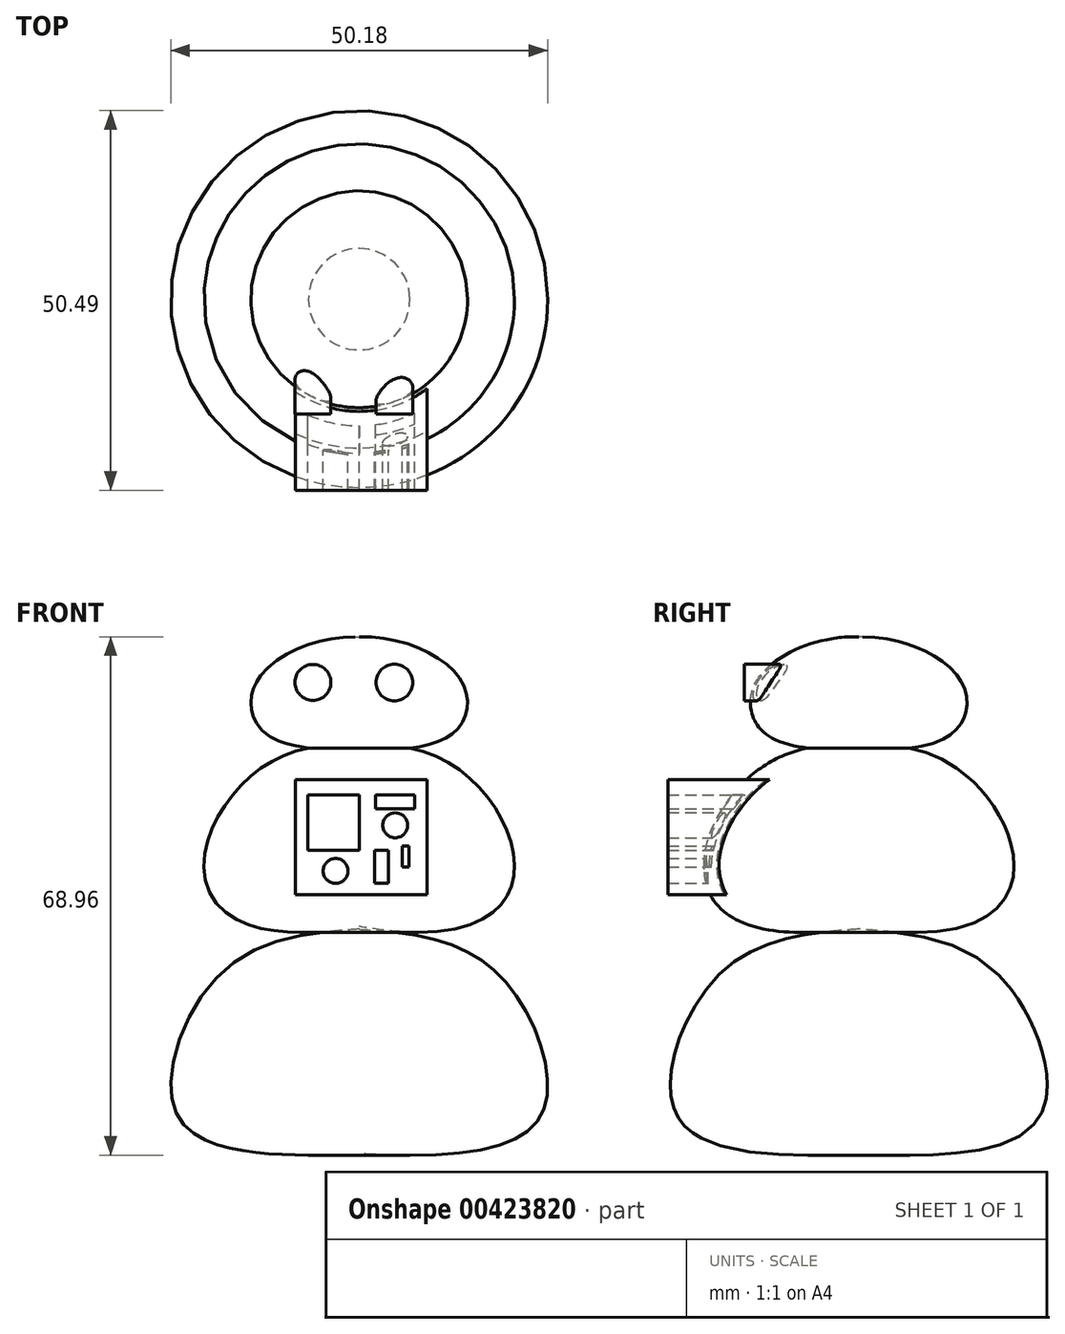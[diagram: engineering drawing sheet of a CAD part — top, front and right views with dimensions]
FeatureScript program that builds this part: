
annotation { "Feature Type Name" : "Feature", "Feature Type Description" : "" }
export const myFeature = defineFeature(function(context is Context, id is Id, definition is map)
    precondition{}
    {
        {
            var Q0;
            Q0=qCreatedBy(makeId("Front.planeOp"),FACE);
            var sketch = newSketch(context, id + "F0", { "sketchPlane" : qUnion([Q0])});
            skLineSegment(sketch, "E0", {"start": v(0, 46.83) * mm, "end": v(0, -37.24) * mm});
            skFitSpline(sketch, "E1", {"points": [v(0, 29.87) * mm, v(19.88, 22.4) * mm, v(24.4, 5.54) * mm, v(0, 0) * mm], "startDerivative": vector(88.45, -5.13) * mm, "endDerivative": vector(-107.1, 5.39) * mm});
            skSolve(sketch);
        }
        {
            var Q0;
            {var subQ0=sQuery(id+"F0.wireOp",EDGE,"E1");Q0=makeQuery(id+"F0.imprint","IMPRINT",FACE,{"disambiguationData":[TD([[makeQuery(id+"F0.imprint","IMPRINT",EDGE,{"derivedFrom":subQ0}),-1.0]])]});}
            var Q1;
            Q1=sQuery(id+"F0.wireOp",EDGE,"E0");
            revolve(context, id + "F1", {"entities" : qUnion([Q0]), "axis" : qUnion([Q1]), "revolveType" : RevolveType.FULL});
        }
        {
            var Q0;
            Q0=qCreatedBy(makeId("Front.planeOp"),FACE);
            var sketch = newSketch(context, id + "F2", { "sketchPlane" : qUnion([Q0])});
            skFitSpline(sketch, "E2", {"points": [v(0, 53.83) * mm, v(16.35, 48.3) * mm, v(20.38, 35.98) * mm, v(0, 30.23) * mm], "startDerivative": vector(62.4, 13.34) * mm, "endDerivative": vector(-104.52, 18.87) * mm});
            skLineSegment(sketch, "E3", {"start": v(0, 59.73) * mm, "end": v(0, -41.3) * mm});
            skLineSegment(sketch, "E4", {"start": v(0.37, -40.19) * mm, "end": v(0, -41.3) * mm});
            skSolve(sketch);
        }
        {
            var Q0;
            {var subQ0=sQuery(id+"F2.wireOp",EDGE,"E2");Q0=makeQuery(id+"F2.imprint","IMPRINT",FACE,{"disambiguationData":[TD([[makeQuery(id+"F2.imprint","IMPRINT",EDGE,{"derivedFrom":subQ0}),-1.0]])]});}
            var Q1;
            Q1=sQuery(id+"F2.wireOp",EDGE,"E3");
            revolve(context, id + "F3", {"entities" : qUnion([Q0]), "axis" : qUnion([Q1]), "revolveType" : RevolveType.FULL});
        }
        {
            var Q0;
            Q0=qCreatedBy(makeId("Front.planeOp"),FACE);
            var sketch = newSketch(context, id + "F4", { "sketchPlane" : qUnion([Q0])});
            skLineSegment(sketch, "E5", {"start": v(0, 74.85) * mm, "end": v(0, -43.14) * mm});
            skFitSpline(sketch, "E6", {"points": [v(0, 68.76) * mm, v(13.72, 62.68) * mm, v(12.62, 56.04) * mm, v(0, 53.65) * mm], "startDerivative": vector(45.1, 1.43) * mm, "endDerivative": vector(-42.53, -0.45) * mm});
            skSolve(sketch);
        }
        {
            var Q0;
            Q0 = qSketchRegion(id + "F4", true);
            var Q1;
            Q1=sQuery(id+"F4.wireOp",EDGE,"E5");
            revolve(context, id + "F5", {"operationType" : NewBodyOperationType.ADD, "entities" : qUnion([Q0]), "axis" : qUnion([Q1]), "revolveType" : RevolveType.FULL});
        }
        {
            var Q0;
            Q0=qCreatedBy(makeId("Front.planeOp"),FACE);
            var sketch = newSketch(context, id + "F6", { "sketchPlane" : qUnion([Q0])});
            skCircle(sketch, "E7", {"center": v(-6.16, 62.7) * mm, "radius": 2.4 * mm});
            skCircle(sketch, "E8", {"center": v(4.69, 62.68) * mm, "radius": 2.45 * mm});
            skSolve(sketch);
        }
        {
            var Q0;
            Q0 = qSketchRegion(id + "F6", true);
            extrude(context, id + "F7", {"entities" : qUnion([Q0]), "operationType" : NewBodyOperationType.ADD, "depth" : 15.24 * mm});
        }
        {
            var Q0;
            Q0=qCreatedBy(makeId("Front.planeOp"),FACE);
            var sketch = newSketch(context, id + "F8", { "sketchPlane" : qUnion([Q0])});
            skLineSegment(sketch, "E9.bottom", {"start": v(-8.48, 49.78) * mm, "end": v(9.03, 49.78) * mm});
            skLineSegment(sketch, "E9.top", {"start": v(-8.48, 34.47) * mm, "end": v(9.03, 34.47) * mm});
            skLineSegment(sketch, "E9.left", {"start": v(-8.48, 49.78) * mm, "end": v(-8.48, 34.47) * mm});
            skLineSegment(sketch, "E9.right", {"start": v(9.03, 49.78) * mm, "end": v(9.03, 34.47) * mm});
            skLineSegment(sketch, "E10.bottom", {"start": v(-6.82, 47.75) * mm, "end": v(0, 47.75) * mm});
            skLineSegment(sketch, "E10.top", {"start": v(-6.82, 40.37) * mm, "end": v(0, 40.37) * mm});
            skLineSegment(sketch, "E10.left", {"start": v(-6.82, 47.75) * mm, "end": v(-6.82, 40.37) * mm});
            skLineSegment(sketch, "E10.right", {"start": v(0, 47.75) * mm, "end": v(0, 40.37) * mm});
            skCircle(sketch, "E11", {"center": v(-5.35, 46.09) * mm, "radius": 1 * mm});
            skCircle(sketch, "E12", {"center": v(-5.35, 42.22) * mm, "radius": 1.1 * mm});
            skLineSegment(sketch, "E13.bottom", {"start": v(-2.77, 46.27) * mm, "end": v(-2.03, 46.27) * mm});
            skLineSegment(sketch, "E13.top", {"start": v(-2.77, 42.03) * mm, "end": v(-2.03, 42.03) * mm});
            skLineSegment(sketch, "E13.left", {"start": v(-2.77, 46.27) * mm, "end": v(-2.77, 42.03) * mm});
            skLineSegment(sketch, "E13.right", {"start": v(-2.03, 46.27) * mm, "end": v(-2.03, 42.03) * mm});
            skLineSegment(sketch, "E14.bottom", {"start": v(2.21, 47.75) * mm, "end": v(7.37, 47.75) * mm});
            skLineSegment(sketch, "E14.top", {"start": v(2.21, 45.9) * mm, "end": v(7.37, 45.9) * mm});
            skLineSegment(sketch, "E14.left", {"start": v(2.21, 47.75) * mm, "end": v(2.21, 45.9) * mm});
            skLineSegment(sketch, "E14.right", {"start": v(7.37, 47.75) * mm, "end": v(7.37, 45.9) * mm});
            skCircle(sketch, "E15", {"center": v(4.8, 43.7) * mm, "radius": 1.66 * mm});
            skPoint(sketch, "E15.centerSnap0", {"position": v(4.8, 45.9) * mm});
            skLineSegment(sketch, "E16.bottom", {"start": v(6.64, 40.93) * mm, "end": v(5.72, 40.93) * mm});
            skLineSegment(sketch, "E16.top", {"start": v(6.64, 38.16) * mm, "end": v(5.72, 38.16) * mm});
            skLineSegment(sketch, "E16.left", {"start": v(6.64, 40.93) * mm, "end": v(6.64, 38.16) * mm});
            skLineSegment(sketch, "E16.right", {"start": v(5.72, 40.93) * mm, "end": v(5.72, 38.16) * mm});
            skLineSegment(sketch, "E17.bottom", {"start": v(2.03, 40.37) * mm, "end": v(3.87, 40.37) * mm});
            skLineSegment(sketch, "E17.top", {"start": v(2.03, 35.95) * mm, "end": v(3.87, 35.95) * mm});
            skLineSegment(sketch, "E17.left", {"start": v(2.03, 40.37) * mm, "end": v(2.03, 35.95) * mm});
            skLineSegment(sketch, "E17.right", {"start": v(3.87, 40.37) * mm, "end": v(3.87, 35.95) * mm});
            skCircle(sketch, "E18", {"center": v(-6.82, 37.6) * mm, "radius": 1.66 * mm});
            skCircle(sketch, "E19", {"center": v(-3.13, 37.6) * mm, "radius": 1.66 * mm});
            skSolve(sketch);
        }
        {
            var Q0;
            Q0 = qSketchRegion(id + "F8", true);
            extrude(context, id + "F9", {"entities" : qUnion([Q0]), "operationType" : NewBodyOperationType.ADD, "depth" : 25.4 * mm});
        }
        {
            var Q0;
            Q0=qCreatedBy(makeId("Front.planeOp"),FACE);
            var sketch = newSketch(context, id + "F10", { "sketchPlane" : qUnion([Q0])});
            skFitSpline(sketch, "E20", {"points": [v(-9.56, 66.67) * mm, v(-6.54, 72.21) * mm, v(12.33, 72.97) * mm, v(14.6, 67.18) * mm, v(10.57, 68.18) * mm, v(12.33, 69.7) * mm, v(8.05, 71.2) * mm, v(6.04, 67.93) * mm, v(5.79, 68.94) * mm], "startDerivative": vector(7.3, 43.13) * mm, "endDerivative": vector(-3.76, 28.78) * mm});
            skSolve(sketch);
        }
        {
            var Q0;
            Q0=sQuery(id+"F10.wireOp",EDGE,"E20");
            extrude(context, id + "F11", {"bodyType" : ToolBodyType.SURFACE, "surfaceEntities" : qUnion([Q0]), "depth" : 12.7 * mm});
        }
    });
